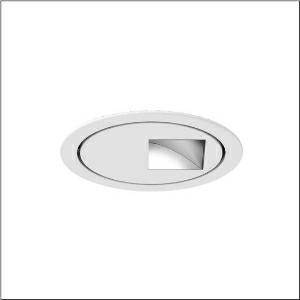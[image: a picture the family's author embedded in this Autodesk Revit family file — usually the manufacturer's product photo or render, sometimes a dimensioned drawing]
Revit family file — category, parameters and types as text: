
# Revit family: lunis_11_mini_round_51dk11cd2wg21
name_source: partatom
category: Lighting Fixtures
units: mm (PartAtom-declared; Revit-internal decimal feet)

## family parameters
Cut with Voids When Loaded = No
Host = Face
Light Source = No
Part Type = Normal
Room Calculation Point = No
Round Connector Dimension = Use Diameter
Shared = No

## types (1)
- Lunis 11 mini round (1 x LED 4000K / CRI = 80 (unbekannt), 2470 lm, 4000K)
    Apparent Load = 28 VA
    CIE Flux Codes = 44 77 97 100 100
    Color Rendering = 80
    Color Temperature = 4000K
    Default Elevation = 1800 mm
    Description = Lunis 11 mini round, downlight, light control with wallwasher, of highly reflective aluminium, highly specular, light emission: direct distribution, LED rated luminous flux: 2.470lm, light colour: 840, control gear: ECG, with terminal, 5-pole, mains connection: 220..230V, AC/DC, 0/50..60Hz, LED module, luminaire module, of aluminium, highly specular, white, diameter: 176mm, clamping range: 1..40mm, recessing ring, of plastic, traffic white (RAL 9016), protection rating (complete): IP20, insulation class (complete): insulation class II (safety insulation), certification: CE, permissible ambient temperature for indoor applications: 0..+35°C, packaging unit: 1 piece
    Height = 0 mm  [stored 0 ft]
    Lamp = 1 x LED 4000K / CRI >= 80 (unbekannt)
    Lamp Light Flux = 2470 lm
    Lamp count = 1
    Length = 176 mm
    Luminous efficacy = 89 lm/W
    Manufacturer = Siteco
    ModVariant = No
    Model = 51DK11CD2WG21
    Mounting Place = Ceiling
    Mounting Type = Recessed
    Number of Poles = 1
    OnlyDefault = Yes
    Power Factor = 1
    Product Name = Lunis 11 mini round
    Product group = downlight
    ProductGroupID = 401
    Protection Class = Protection class II
    Protection Degree = IP 20
    RLX_Detail_Level = 1
    RLX_Emergency_Light_Flux = 0 lm
    RLX_Emergency_Type = 0
    RLX_Emergency_Type_DB = No
    RlxData = <blob elided: 59469 chars, md5=7854d969>
    Socket = socket
    Standby Power = 0 W
    System Light Flux = 2470 lm
    System Power = 28 W
    Type Comments = Product without accessories
    Type Image = l_1004772.jpg
    URL = http://relux.com
    VarID = ---
    Voltage = 0 V
    Weight = 0.00 kg
    Width = 176 mm

note: [stored X ft] marks values corroborated as IEEE doubles in the binary element streams (Revit-internal decimal feet)

## geometry (parser evidence)
native form markers: Blend x4, Sweep x11
no freeform markers — native parametric forms only
